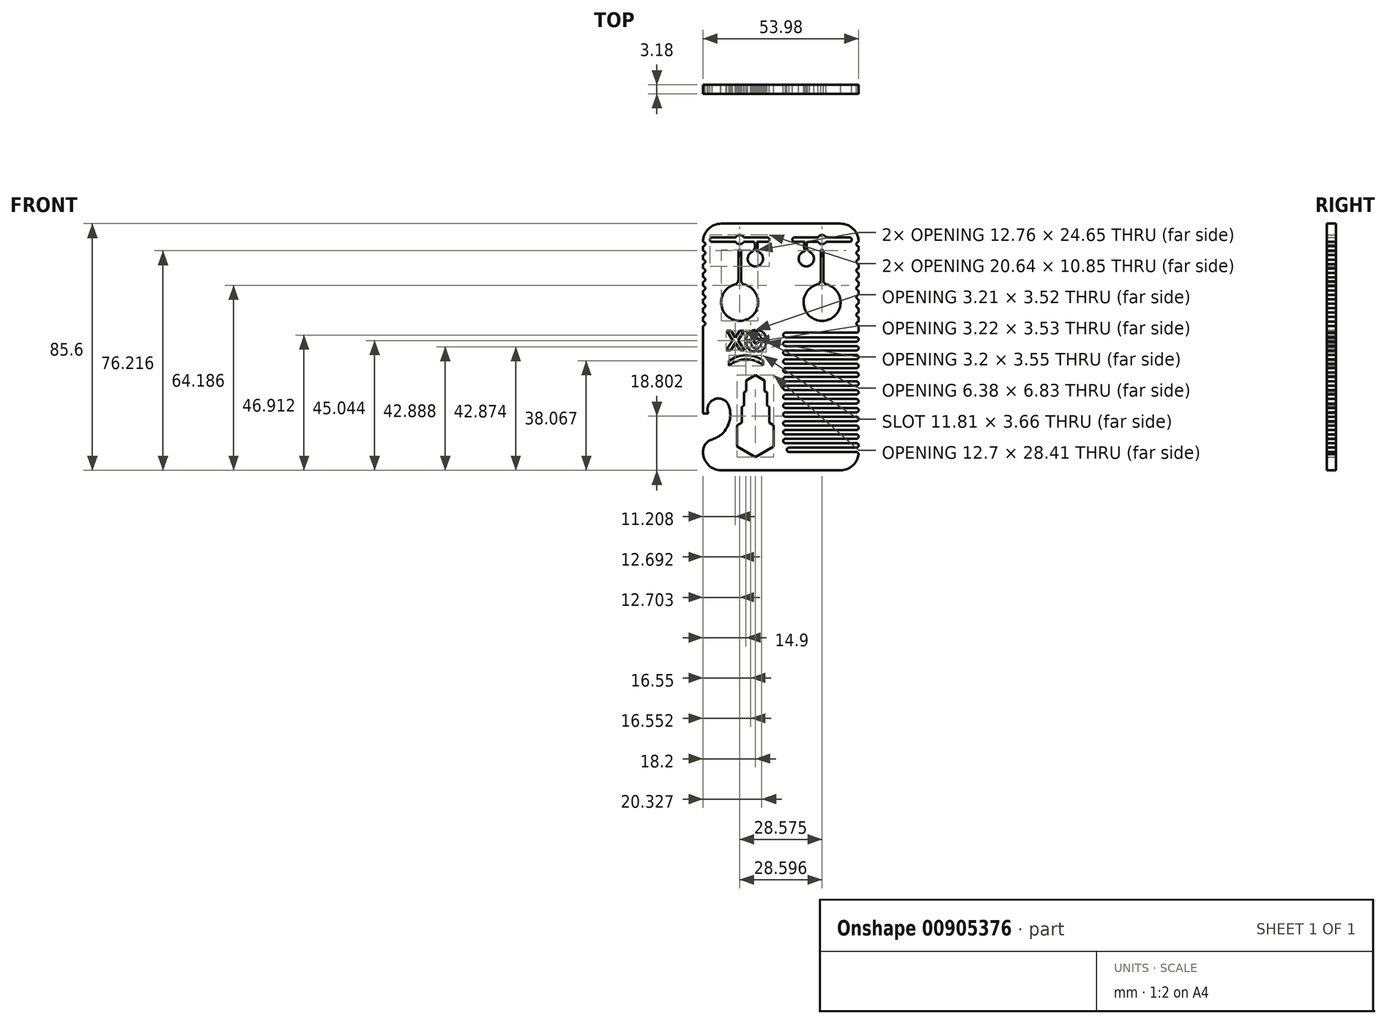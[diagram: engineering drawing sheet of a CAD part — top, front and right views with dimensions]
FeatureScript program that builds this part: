
annotation { "Feature Type Name" : "Feature", "Feature Type Description" : "" }
export const myFeature = defineFeature(function(context is Context, id is Id, definition is map)
    precondition{}
    {
        {
            var Q0;
            Q0=qCreatedBy(makeId("Front.planeOp"),FACE);
            var sketch = newSketch(context, id + "F0", { "sketchPlane" : qUnion([Q0])});
            skLineSegment(sketch, "E0.bottom", {"start": v(-17.87, 77.8) * mm, "end": v(23.4, 77.8) * mm});
            skLineSegment(sketch, "E0.top", {"start": v(-99.66, -7.8) * mm, "end": v(-99.66, -7.58) * mm});
            skLineSegment(sketch, "E0.left", {"start": v(-24.22, 69.91) * mm, "end": v(-24.22, 68.38) * mm});
            skLineSegment(sketch, "E0.right", {"start": v(29.76, 69.91) * mm, "end": v(29.76, 68.38) * mm});
            skPoint(sketch, "E1.visualSharp", {"position": v(-45.91, 65.1) * mm});
            skArc(sketch, "E1.filletArc", {"start": v(-17.87, 77.8) * mm, "mid": v(-22.36, 75.94) * mm, "end": v(-24.22, 71.45) * mm});
            skArc(sketch, "E2.filletArc", {"start": v(29.76, 71.45) * mm, "mid": v(27.9, 75.94) * mm, "end": v(23.4, 77.8) * mm});
            skPoint(sketch, "E3.visualSharp", {"position": v(29.76, -7.8) * mm});
            skArc(sketch, "E3.filletArc", {"start": v(23.4, -7.8) * mm, "mid": v(27.65, -6.17) * mm, "end": v(29.72, -2.12) * mm});
            skPoint(sketch, "E4.visualSharp", {"position": v(-24.22, -7.8) * mm});
            skArc(sketch, "E4.filletArc", {"start": v(-24.22, -1.45) * mm, "mid": v(-22.36, -5.94) * mm, "end": v(-17.87, -7.8) * mm});
            skLineSegment(sketch, "E5", {"start": v(-21.04, 71.45) * mm, "end": v(-21.04, 72.24) * mm});
            skLineSegment(sketch, "E6", {"start": v(-21.04, 73.03) * mm, "end": v(-13.12, 73.03) * mm});
            skLineSegment(sketch, "E7", {"start": v(-2, 72.24) * mm, "end": v(-2, 71.45) * mm});
            skPoint(sketch, "E8.center.orphan", {"position": v(2.77, -7.8) * mm});
            skLineSegment(sketch, "E9", {"start": v(-21.04, 71.45) * mm, "end": v(-12.9, 71.45) * mm});
            skLineSegment(sketch, "E10.trimOffspring", {"start": v(-4.44, -7.8) * mm, "end": v(23.4, -7.8) * mm});
            skArc(sketch, "E11", {"start": v(74.74, 43.3) * mm, "mid": v(66.07, 45.82) * mm, "end": v(57.48, 43.05) * mm});
            skLineSegment(sketch, "E12.MirrorCS", {"start": v(-10.76, 60.6) * mm, "end": v(-10.76, 60.6) * mm});
            skLineSegment(sketch, "E13.MirrorCS", {"start": v(-12.3, 60.6) * mm, "end": v(-12.3, 60.6) * mm});
            skArc(sketch, "E14", {"start": v(69.27, 55.85) * mm, "mid": v(68.77, 54.72) * mm, "end": v(68.53, 53.5) * mm});
            skArc(sketch, "E15", {"start": v(68.72, 51.54) * mm, "mid": v(69.46, 50.16) * mm, "end": v(70.87, 49.5) * mm});
            skArc(sketch, "E16", {"start": v(70.87, 58.64) * mm, "mid": v(70.16, 58.57) * mm, "end": v(69.47, 58.42) * mm});
            skArc(sketch, "E17", {"start": v(69.47, 58.42) * mm, "mid": v(68.6, 58.07) * mm, "end": v(67.84, 57.55) * mm});
            skArc(sketch, "E18", {"start": v(67.84, 57.55) * mm, "mid": v(67.12, 56.76) * mm, "end": v(66.62, 55.81) * mm});
            skArc(sketch, "E19", {"start": v(66.62, 55.81) * mm, "mid": v(66.3, 54.68) * mm, "end": v(66.18, 53.5) * mm});
            skArc(sketch, "E20", {"start": v(66.18, 53.5) * mm, "mid": v(66.18, 53.5) * mm, "end": v(66.18, 53.5) * mm});
            skArc(sketch, "E21", {"start": v(66.25, 51.87) * mm, "mid": v(66.4, 51.1) * mm, "end": v(66.64, 50.36) * mm});
            skArc(sketch, "E22", {"start": v(66.64, 50.36) * mm, "mid": v(66.92, 49.77) * mm, "end": v(67.29, 49.24) * mm});
            skArc(sketch, "E23", {"start": v(67.29, 49.24) * mm, "mid": v(67.8, 48.7) * mm, "end": v(68.4, 48.27) * mm});
            skArc(sketch, "E24", {"start": v(68.4, 48.27) * mm, "mid": v(69.1, 47.94) * mm, "end": v(69.84, 47.73) * mm});
            skArc(sketch, "E25", {"start": v(69.84, 47.73) * mm, "mid": v(70.31, 47.64) * mm, "end": v(70.8, 47.6) * mm});
            skArc(sketch, "E26", {"start": v(70.8, 47.6) * mm, "mid": v(70.83, 47.6) * mm, "end": v(70.87, 47.6) * mm});
            skLineSegment(sketch, "E27", {"start": v(71.26, 56.74) * mm, "end": v(71.26, 56.75) * mm});
            skLineSegment(sketch, "E28", {"start": v(71.28, 49.47) * mm, "end": v(71.28, 49.46) * mm});
            skLineSegment(sketch, "E29.trimOffspring", {"start": v(70.87, 56.7) * mm, "end": v(70.87, 58.65) * mm});
            skLineSegment(sketch, "E30", {"start": v(70.87, 48.55) * mm, "end": v(70.87, 47.6) * mm});
            skArc(sketch, "E31.trimOffspring", {"start": v(71.28, 47.58) * mm, "mid": v(71.3, 47.58) * mm, "end": v(71.3, 47.58) * mm});
            skLineSegment(sketch, "E32.trimOffspring", {"start": v(70.87, 49.5) * mm, "end": v(70.87, 48.55) * mm});
            skArc(sketch, "E33.trimOffspring", {"start": v(70.87, 56.7) * mm, "mid": v(70, 56.42) * mm, "end": v(69.27, 55.85) * mm});
            skPoint(sketch, "E34.orphan", {"position": v(68.51, 52.97) * mm});
            skLineSegment(sketch, "E35", {"start": v(71.26, 56.75) * mm, "end": v(71.26, 56.74) * mm});
            skArc(sketch, "E36.MirrorCS", {"start": v(71.64, 56.71) * mm, "mid": v(72.52, 56.43) * mm, "end": v(73.25, 55.87) * mm});
            skArc(sketch, "E37.MirrorCS", {"start": v(73.25, 55.87) * mm, "mid": v(73.77, 54.75) * mm, "end": v(74.01, 53.53) * mm});
            skArc(sketch, "E38.MirrorCS", {"start": v(73.84, 51.56) * mm, "mid": v(73.12, 50.17) * mm, "end": v(71.7, 49.5) * mm});
            skArc(sketch, "E39.MirrorCS", {"start": v(71.8, 47.6) * mm, "mid": v(71.77, 47.6) * mm, "end": v(71.73, 47.6) * mm});
            skArc(sketch, "E40.MirrorCS", {"start": v(72.76, 47.74) * mm, "mid": v(72.29, 47.65) * mm, "end": v(71.8, 47.6) * mm});
            skArc(sketch, "E41.MirrorCS", {"start": v(74.19, 48.3) * mm, "mid": v(73.5, 47.96) * mm, "end": v(72.76, 47.74) * mm});
            skArc(sketch, "E42.MirrorCS", {"start": v(75.3, 49.28) * mm, "mid": v(74.79, 48.73) * mm, "end": v(74.19, 48.3) * mm});
            skArc(sketch, "E43.MirrorCS", {"start": v(75.94, 50.4) * mm, "mid": v(75.66, 49.81) * mm, "end": v(75.3, 49.28) * mm});
            skArc(sketch, "E44.MirrorCS", {"start": v(76.3, 51.92) * mm, "mid": v(76.17, 51.15) * mm, "end": v(75.94, 50.4) * mm});
            skArc(sketch, "E45.MirrorCS", {"start": v(76.37, 53.55) * mm, "mid": v(76.37, 53.55) * mm, "end": v(76.37, 53.54) * mm});
            skArc(sketch, "E46.MirrorCS", {"start": v(75.9, 55.86) * mm, "mid": v(76.23, 54.73) * mm, "end": v(76.37, 53.55) * mm});
            skArc(sketch, "E47.MirrorCS", {"start": v(74.66, 57.58) * mm, "mid": v(75.39, 56.8) * mm, "end": v(75.9, 55.86) * mm});
            skArc(sketch, "E48.MirrorCS", {"start": v(73.02, 58.43) * mm, "mid": v(73.9, 58.1) * mm, "end": v(74.66, 57.58) * mm});
            skArc(sketch, "E49.MirrorCS", {"start": v(71.63, 58.65) * mm, "mid": v(72.33, 58.58) * mm, "end": v(73.02, 58.43) * mm});
            skLineSegment(sketch, "E50.MirrorCS", {"start": v(71.64, 56.71) * mm, "end": v(71.63, 58.65) * mm});
            skLineSegment(sketch, "E51.MirrorCS", {"start": v(71.7, 49.5) * mm, "end": v(71.72, 48.55) * mm});
            skLineSegment(sketch, "E52.MirrorCS", {"start": v(71.72, 48.55) * mm, "end": v(71.73, 47.6) * mm});
            skArc(sketch, "E53", {"start": v(71.28, 49.46) * mm, "mid": v(71.29, 49.46) * mm, "end": v(71.3, 49.46) * mm});
            skLineSegment(sketch, "E54.0", {"start": v(66.17, 52.73) * mm, "end": v(68.52, 52.75) * mm});
            skLineSegment(sketch, "E55.0", {"start": v(66.16, 53.5) * mm, "end": v(68.53, 53.5) * mm});
            skLineSegment(sketch, "E56.trimOffspring", {"start": v(74.01, 53.53) * mm, "end": v(76.38, 53.55) * mm});
            skPoint(sketch, "E57.orphan", {"position": v(71.27, 53.12) * mm});
            skLineSegment(sketch, "E58.trimOffspring", {"start": v(74.03, 52.77) * mm, "end": v(76.38, 52.78) * mm});
            skPoint(sketch, "E59.MirrorCS.end.orphan", {"position": v(71.3, 49.46) * mm});
            skPoint(sketch, "E59.MirrorCS.start.orphan", {"position": v(71.7, 49.5) * mm});
            skPoint(sketch, "E60.MirrorCS.end.orphan", {"position": v(72.06, 47.58) * mm});
            skPoint(sketch, "E60.MirrorCS.start.orphan", {"position": v(72.49, 47.6) * mm});
            skPoint(sketch, "E61.orphan", {"position": v(71.25, 58.65) * mm});
            skPoint(sketch, "E62.MirrorCS.end.orphan", {"position": v(71.64, 56.71) * mm});
            skArc(sketch, "E63.trimOffspring", {"start": v(66.17, 52.73) * mm, "mid": v(66.2, 52.3) * mm, "end": v(66.25, 51.87) * mm});
            skArc(sketch, "E64.trimOffspring", {"start": v(68.52, 52.75) * mm, "mid": v(68.59, 52.14) * mm, "end": v(68.72, 51.54) * mm});
            skArc(sketch, "E65.trimOffspring", {"start": v(74.03, 52.77) * mm, "mid": v(73.97, 52.16) * mm, "end": v(73.84, 51.56) * mm});
            skArc(sketch, "E66.trimOffspring", {"start": v(76.38, 52.78) * mm, "mid": v(76.36, 52.35) * mm, "end": v(76.3, 51.92) * mm});
            skText(sketch, "E67", { "text": "X", "fontName": "OpenSans-Bold.ttf"});
            skArc(sketch, "E68", {"start": v(-101.45, 5.62) * mm, "mid": v(-103.88, 10.61) * mm, "end": v(-108.72, 7.88) * mm});
            skArc(sketch, "E69", {"start": v(-99.66, -7.58) * mm, "mid": v(-100.52, -4.97) * mm, "end": v(-102.78, -3.42) * mm});
            skArc(sketch, "E70", {"start": v(-108.72, 7.88) * mm, "mid": v(-108.7, 2.5) * mm, "end": v(-105.7, -1.96) * mm});
            skArc(sketch, "E71", {"start": v(-105.7, -1.96) * mm, "mid": v(-104.29, -2.8) * mm, "end": v(-102.78, -3.42) * mm});
            skLineSegment(sketch, "E72", {"start": v(-101.45, 5.62) * mm, "end": v(-99.66, 5.62) * mm});
            skLineSegment(sketch, "E73", {"start": v(-10.77, 56.83) * mm, "end": v(-10.76, 56.83) * mm});
            skLineSegment(sketch, "E74", {"start": v(29.76, 41.39) * mm, "end": v(29.76, 42.32) * mm});
            skLineSegment(sketch, "E75", {"start": v(5.61, 0.07) * mm, "end": v(29, 0.07) * mm});
            skArc(sketch, "E76", {"start": v(29, 0.07) * mm, "mid": v(29.76, 0.84) * mm, "end": v(29, 1.6) * mm});
            skLineSegment(sketch, "E77", {"start": v(29, 1.6) * mm, "end": v(4.36, 1.6) * mm});
            skArc(sketch, "E78", {"start": v(29.72, -2.12) * mm, "mid": v(29.49, -1.65) * mm, "end": v(29, -1.46) * mm});
            skPoint(sketch, "E79.start.orphan", {"position": v(29.76, -1.45) * mm});
            skArc(sketch, "E80", {"start": v(5.61, 0.07) * mm, "mid": v(4.86, -0.7) * mm, "end": v(5.61, -1.46) * mm});
            skLineSegment(sketch, "E81", {"start": v(5.61, -1.46) * mm, "end": v(29, -1.46) * mm});
            skArc(sketch, "E82", {"start": v(4.36, 3.14) * mm, "mid": v(3.6, 2.37) * mm, "end": v(4.36, 1.6) * mm});
            skLineSegment(sketch, "E83", {"start": v(4.36, 3.14) * mm, "end": v(29, 3.14) * mm});
            skArc(sketch, "E84", {"start": v(29, 3.14) * mm, "mid": v(29.76, 3.9) * mm, "end": v(29, 4.67) * mm});
            skLineSegment(sketch, "E85", {"start": v(29, 4.67) * mm, "end": v(4.36, 4.67) * mm});
            skLineSegment(sketch, "E86", {"start": v(4.36, 6.2) * mm, "end": v(29, 6.2) * mm});
            skArc(sketch, "E87", {"start": v(29, 6.2) * mm, "mid": v(29.76, 6.97) * mm, "end": v(29, 7.74) * mm});
            skLineSegment(sketch, "E88", {"start": v(29, 7.74) * mm, "end": v(4.36, 7.74) * mm});
            skArc(sketch, "E89", {"start": v(4.36, 9.27) * mm, "mid": v(3.6, 8.5) * mm, "end": v(4.36, 7.74) * mm});
            skLineSegment(sketch, "E90", {"start": v(4.36, 9.27) * mm, "end": v(29, 9.27) * mm});
            skArc(sketch, "E91", {"start": v(29, 9.27) * mm, "mid": v(29.76, 10.04) * mm, "end": v(29, 10.8) * mm});
            skLineSegment(sketch, "E92", {"start": v(29, 10.8) * mm, "end": v(4.36, 10.8) * mm});
            skLineSegment(sketch, "E93", {"start": v(4.36, 12.34) * mm, "end": v(29, 12.34) * mm});
            skArc(sketch, "E94", {"start": v(29, 12.34) * mm, "mid": v(29.76, 13.1) * mm, "end": v(29, 13.87) * mm});
            skLineSegment(sketch, "E95", {"start": v(29, 13.87) * mm, "end": v(4.36, 13.87) * mm});
            skArc(sketch, "E96", {"start": v(4.36, 12.34) * mm, "mid": v(3.6, 11.57) * mm, "end": v(4.36, 10.8) * mm});
            skArc(sketch, "E97", {"start": v(4.36, 15.4) * mm, "mid": v(3.6, 14.64) * mm, "end": v(4.36, 13.87) * mm});
            skLineSegment(sketch, "E98", {"start": v(4.36, 15.4) * mm, "end": v(29, 15.4) * mm});
            skArc(sketch, "E99", {"start": v(29, 15.4) * mm, "mid": v(29.76, 16.17) * mm, "end": v(29, 16.94) * mm});
            skLineSegment(sketch, "E100", {"start": v(29, 16.94) * mm, "end": v(4.36, 16.94) * mm});
            skArc(sketch, "E101", {"start": v(4.36, 18.47) * mm, "mid": v(3.6, 17.7) * mm, "end": v(4.36, 16.94) * mm});
            skLineSegment(sketch, "E102", {"start": v(4.36, 18.47) * mm, "end": v(29, 18.47) * mm});
            skArc(sketch, "E103", {"start": v(29, 18.47) * mm, "mid": v(29.76, 19.24) * mm, "end": v(29, 20) * mm});
            skLineSegment(sketch, "E104", {"start": v(29, 20) * mm, "end": v(4.36, 20) * mm});
            skArc(sketch, "E105", {"start": v(4.36, 21.53) * mm, "mid": v(3.6, 20.77) * mm, "end": v(4.36, 20) * mm});
            skLineSegment(sketch, "E106", {"start": v(4.36, 21.53) * mm, "end": v(29, 21.53) * mm});
            skArc(sketch, "E107", {"start": v(29, 21.53) * mm, "mid": v(29.76, 22.3) * mm, "end": v(29, 23.07) * mm});
            skLineSegment(sketch, "E108", {"start": v(29, 23.07) * mm, "end": v(4.36, 23.07) * mm});
            skArc(sketch, "E109", {"start": v(4.36, 24.6) * mm, "mid": v(3.6, 23.83) * mm, "end": v(4.36, 23.07) * mm});
            skLineSegment(sketch, "E110", {"start": v(4.36, 24.6) * mm, "end": v(29, 24.6) * mm});
            skArc(sketch, "E111", {"start": v(29, 24.6) * mm, "mid": v(29.76, 25.37) * mm, "end": v(29, 26.13) * mm});
            skLineSegment(sketch, "E112", {"start": v(29, 26.13) * mm, "end": v(4.36, 26.13) * mm});
            skArc(sketch, "E113", {"start": v(4.36, 27.67) * mm, "mid": v(3.6, 26.9) * mm, "end": v(4.36, 26.13) * mm});
            skLineSegment(sketch, "E114", {"start": v(4.36, 27.67) * mm, "end": v(29, 27.67) * mm});
            skArc(sketch, "E115", {"start": v(29, 27.67) * mm, "mid": v(29.76, 28.43) * mm, "end": v(29, 29.2) * mm});
            skLineSegment(sketch, "E116", {"start": v(29, 29.2) * mm, "end": v(4.36, 29.2) * mm});
            skArc(sketch, "E117", {"start": v(4.36, 30.73) * mm, "mid": v(3.6, 29.97) * mm, "end": v(4.36, 29.2) * mm});
            skLineSegment(sketch, "E118", {"start": v(4.36, 30.73) * mm, "end": v(29, 30.73) * mm});
            skArc(sketch, "E119", {"start": v(29, 30.73) * mm, "mid": v(29.76, 31.5) * mm, "end": v(29, 32.26) * mm});
            skLineSegment(sketch, "E120", {"start": v(29, 32.26) * mm, "end": v(4.36, 32.26) * mm});
            skArc(sketch, "E121", {"start": v(4.36, 33.8) * mm, "mid": v(3.6, 33.03) * mm, "end": v(4.36, 32.26) * mm});
            skLineSegment(sketch, "E122", {"start": v(4.36, 33.8) * mm, "end": v(29, 33.8) * mm});
            skArc(sketch, "E123", {"start": v(29, 33.8) * mm, "mid": v(29.76, 34.56) * mm, "end": v(29, 35.33) * mm});
            skLineSegment(sketch, "E124", {"start": v(29, 35.33) * mm, "end": v(4.36, 35.33) * mm});
            skArc(sketch, "E125", {"start": v(4.36, 36.86) * mm, "mid": v(3.6, 36.1) * mm, "end": v(4.36, 35.33) * mm});
            skLineSegment(sketch, "E126", {"start": v(4.36, 36.86) * mm, "end": v(29, 36.86) * mm});
            skArc(sketch, "E127", {"start": v(29, 36.86) * mm, "mid": v(29.76, 37.63) * mm, "end": v(29, 38.4) * mm});
            skLineSegment(sketch, "E128", {"start": v(29, 38.4) * mm, "end": v(4.36, 38.4) * mm});
            skArc(sketch, "E129", {"start": v(4.36, 39.93) * mm, "mid": v(3.6, 39.16) * mm, "end": v(4.36, 38.4) * mm});
            skLineSegment(sketch, "E130", {"start": v(4.36, 39.93) * mm, "end": v(29, 39.93) * mm});
            skArc(sketch, "E131", {"start": v(29, 39.93) * mm, "mid": v(29.54, 40.16) * mm, "end": v(29.76, 40.7) * mm});
            skLineSegment(sketch, "E132", {"start": v(29.76, 40.7) * mm, "end": v(29.76, 41.39) * mm});
            skLineSegment(sketch, "E133.0", {"start": v(-11.98, 68.27) * mm, "end": v(-11.98, 58.2) * mm});
            skLineSegment(sketch, "E134.0", {"start": v(-11.09, 68.27) * mm, "end": v(-11.09, 58.2) * mm});
            skArc(sketch, "E135", {"start": v(-12.9, 56.75) * mm, "mid": v(-11.52, 44.06) * mm, "end": v(-10.16, 56.75) * mm});
            skArc(sketch, "E136", {"start": v(-24.22, 42.32) * mm, "mid": v(-23.46, 43.09) * mm, "end": v(-24.22, 43.85) * mm});
            skArc(sketch, "E137", {"start": v(-24.22, 45.39) * mm, "mid": v(-23.46, 46.15) * mm, "end": v(-24.22, 46.92) * mm});
            skArc(sketch, "E138", {"start": v(-24.22, 48.45) * mm, "mid": v(-23.46, 49.22) * mm, "end": v(-24.22, 49.99) * mm});
            skArc(sketch, "E139", {"start": v(-24.22, 51.52) * mm, "mid": v(-23.46, 52.28) * mm, "end": v(-24.22, 53.05) * mm});
            skArc(sketch, "E140", {"start": v(-24.22, 54.58) * mm, "mid": v(-23.46, 55.35) * mm, "end": v(-24.22, 56.12) * mm});
            skArc(sketch, "E141", {"start": v(-24.22, 57.65) * mm, "mid": v(-23.46, 58.42) * mm, "end": v(-24.22, 59.18) * mm});
            skArc(sketch, "E142", {"start": v(-24.22, 60.72) * mm, "mid": v(-23.46, 61.48) * mm, "end": v(-24.22, 62.25) * mm});
            skArc(sketch, "E143", {"start": v(-24.22, 63.78) * mm, "mid": v(-23.46, 64.55) * mm, "end": v(-24.22, 65.31) * mm});
            skArc(sketch, "E144", {"start": v(-24.22, 66.85) * mm, "mid": v(-23.46, 67.61) * mm, "end": v(-24.22, 68.38) * mm});
            skArc(sketch, "E145", {"start": v(-24.22, 69.91) * mm, "mid": v(-23.46, 70.68) * mm, "end": v(-24.22, 71.45) * mm});
            skArc(sketch, "E146", {"start": v(29.76, 43.85) * mm, "mid": v(29, 43.09) * mm, "end": v(29.76, 42.32) * mm});
            skArc(sketch, "E147", {"start": v(29.76, 46.92) * mm, "mid": v(29, 46.15) * mm, "end": v(29.76, 45.39) * mm});
            skArc(sketch, "E148", {"start": v(29.76, 49.99) * mm, "mid": v(29, 49.22) * mm, "end": v(29.76, 48.45) * mm});
            skArc(sketch, "E149", {"start": v(29.76, 53.05) * mm, "mid": v(29, 52.28) * mm, "end": v(29.76, 51.52) * mm});
            skArc(sketch, "E150", {"start": v(29.76, 56.12) * mm, "mid": v(29, 55.35) * mm, "end": v(29.76, 54.58) * mm});
            skArc(sketch, "E151", {"start": v(29.76, 59.18) * mm, "mid": v(29, 58.42) * mm, "end": v(29.76, 57.65) * mm});
            skArc(sketch, "E152", {"start": v(29.76, 62.25) * mm, "mid": v(29, 61.48) * mm, "end": v(29.76, 60.72) * mm});
            skArc(sketch, "E153", {"start": v(29.76, 65.31) * mm, "mid": v(29, 64.55) * mm, "end": v(29.76, 63.78) * mm});
            skArc(sketch, "E154", {"start": v(29.76, 68.38) * mm, "mid": v(29, 67.61) * mm, "end": v(29.76, 66.85) * mm});
            skArc(sketch, "E155", {"start": v(29.76, 71.45) * mm, "mid": v(29, 70.68) * mm, "end": v(29.76, 69.91) * mm});
            skLineSegment(sketch, "E156.trimOffspring", {"start": v(-24.22, 45.39) * mm, "end": v(-24.22, 43.85) * mm});
            skLineSegment(sketch, "E157.trimOffspring", {"start": v(-24.22, 48.45) * mm, "end": v(-24.22, 46.92) * mm});
            skLineSegment(sketch, "E158.trimOffspring", {"start": v(-24.22, 51.52) * mm, "end": v(-24.22, 49.99) * mm});
            skLineSegment(sketch, "E159.trimOffspring", {"start": v(-24.22, 54.58) * mm, "end": v(-24.22, 53.05) * mm});
            skLineSegment(sketch, "E160.trimOffspring", {"start": v(-24.22, 57.65) * mm, "end": v(-24.22, 56.12) * mm});
            skLineSegment(sketch, "E161.trimOffspring", {"start": v(-24.22, 60.72) * mm, "end": v(-24.22, 59.18) * mm});
            skLineSegment(sketch, "E162.trimOffspring", {"start": v(-24.22, 63.78) * mm, "end": v(-24.22, 62.25) * mm});
            skLineSegment(sketch, "E163.trimOffspring", {"start": v(-24.22, 66.85) * mm, "end": v(-24.22, 65.31) * mm});
            skLineSegment(sketch, "E164.trimOffspring", {"start": v(29.76, 66.85) * mm, "end": v(29.76, 65.31) * mm});
            skLineSegment(sketch, "E165.trimOffspring", {"start": v(29.76, 63.78) * mm, "end": v(29.76, 62.25) * mm});
            skLineSegment(sketch, "E166.trimOffspring", {"start": v(29.76, 60.72) * mm, "end": v(29.76, 59.18) * mm});
            skLineSegment(sketch, "E167.trimOffspring", {"start": v(29.76, 57.65) * mm, "end": v(29.76, 56.12) * mm});
            skLineSegment(sketch, "E168.trimOffspring", {"start": v(29.76, 54.58) * mm, "end": v(29.76, 53.05) * mm});
            skLineSegment(sketch, "E169.trimOffspring", {"start": v(29.76, 51.52) * mm, "end": v(29.76, 49.99) * mm});
            skLineSegment(sketch, "E170.trimOffspring", {"start": v(29.76, 48.45) * mm, "end": v(29.76, 46.92) * mm});
            skLineSegment(sketch, "E171.trimOffspring", {"start": v(29.76, 45.39) * mm, "end": v(29.76, 43.85) * mm});
            skLineSegment(sketch, "E172", {"start": v(74.74, 40.78) * mm, "end": v(74.74, 43.3) * mm});
            skLineSegment(sketch, "E173", {"start": v(74.74, 43.3) * mm, "end": v(74.74, 40.78) * mm});
            skCircle(sketch, "E174", {"center": v(71.27, 53.12) * mm, "radius": 1.3 * mm});
            skPoint(sketch, "E175.orphan", {"position": v(-11.53, 68.27) * mm});
            skLineSegment(sketch, "E176.trimOffspring", {"start": v(-9.94, 73.03) * mm, "end": v(-2, 73.03) * mm});
            skLineSegment(sketch, "E177", {"start": v(-13.12, 73.03) * mm, "end": v(-12.9, 73.03) * mm});
            skArc(sketch, "E178.MirrorCS", {"start": v(-12.9, 73.03) * mm, "mid": v(-11.52, 73.84) * mm, "end": v(-10.13, 73.03) * mm});
            skArc(sketch, "E179.MirrorCS", {"start": v(-10.13, 71.45) * mm, "mid": v(-11.52, 70.64) * mm, "end": v(-12.9, 71.45) * mm});
            skPoint(sketch, "E180.start.orphan", {"position": v(2.77, 77.8) * mm});
            skLineSegment(sketch, "E181.trimOffspring", {"start": v(-10.13, 71.45) * mm, "end": v(-6.5, 71.45) * mm});
            skLineSegment(sketch, "E182.trimOffspring", {"start": v(-10.13, 73.03) * mm, "end": v(-9.94, 73.03) * mm});
            skLineSegment(sketch, "E183.trimOffspring", {"start": v(-5.52, 71.45) * mm, "end": v(-2, 71.45) * mm});
            skArc(sketch, "E184", {"start": v(-7.14, 68.04) * mm, "mid": v(-6.18, 69.62) * mm, "end": v(-6.5, 71.45) * mm});
            skArc(sketch, "E185.0", {"start": v(-5.63, 68.52) * mm, "mid": v(-5.25, 69.97) * mm, "end": v(-5.52, 71.45) * mm});
            skPoint(sketch, "E186.start.orphan", {"position": v(-7.14, 68.04) * mm});
            skArc(sketch, "E187.MirrorCS", {"start": v(-7.14, 68.04) * mm, "mid": v(-5.8, 63) * mm, "end": v(-5.48, 68.2) * mm});
            skPoint(sketch, "E188.orphan", {"position": v(-7.17, 68.02) * mm});
            skArc(sketch, "E189.0", {"start": v(74.74, 40.78) * mm, "mid": v(66.06, 43.78) * mm, "end": v(57.48, 40.47) * mm});
            skLineSegment(sketch, "E190", {"start": v(57.48, 43.05) * mm, "end": v(57.48, 40.47) * mm});
            skArc(sketch, "E191", {"start": v(-5.63, 68.52) * mm, "mid": v(-5.62, 68.32) * mm, "end": v(-5.48, 68.2) * mm});
            skLineSegment(sketch, "E192.0", {"start": v(-24.15, -14.77) * mm, "end": v(-19.6, -14.16) * mm});
            skLineSegment(sketch, "E192.1", {"start": v(-19.6, -14.16) * mm, "end": v(-16.8, -17.8) * mm});
            skArc(sketch, "E193", {"start": v(4.36, 6.2) * mm, "mid": v(3.6, 5.44) * mm, "end": v(4.36, 4.67) * mm});
            skLineSegment(sketch, "E194.0", {"start": v(0.33, 0.46) * mm, "end": v(-6.02, -3.2) * mm});
            skLineSegment(sketch, "E194.1", {"start": v(-6.02, -3.2) * mm, "end": v(-12.37, 0.46) * mm});
            skLineSegment(sketch, "E194.2", {"start": v(-12.37, 0.46) * mm, "end": v(-12.37, 7.8) * mm});
            skLineSegment(sketch, "E194.3", {"start": v(-12.37, 7.8) * mm, "end": v(-10.78, 8.71) * mm});
            skLineSegment(sketch, "E194.4", {"start": v(-1.26, 8.71) * mm, "end": v(0.33, 7.8) * mm});
            skLineSegment(sketch, "E194.5", {"start": v(0.33, 7.8) * mm, "end": v(0.33, 0.46) * mm});
            skPoint(sketch, "E194.0.midPoint", {"position": v(-2.84, -1.37) * mm});
            skLineSegment(sketch, "E195.2", {"start": v(-10.78, 8.71) * mm, "end": v(-10.78, 14.2) * mm});
            skLineSegment(sketch, "E195.3", {"start": v(-10.78, 14.2) * mm, "end": v(-9.99, 14.67) * mm});
            skLineSegment(sketch, "E195.4", {"start": v(-2.05, 14.67) * mm, "end": v(-1.26, 14.2) * mm});
            skLineSegment(sketch, "E195.5", {"start": v(-1.26, 14.2) * mm, "end": v(-1.26, 8.71) * mm});
            skPoint(sketch, "E195.0.midPoint", {"position": v(-3.64, 7.34) * mm});
            skPoint(sketch, "E196.visualSharp", {"position": v(-6.55, 6.45) * mm});
            skLineSegment(sketch, "E197.2", {"start": v(-9.99, 14.67) * mm, "end": v(-9.99, 19.25) * mm});
            skLineSegment(sketch, "E197.3", {"start": v(-9.99, 19.25) * mm, "end": v(-9.2, 19.7) * mm});
            skLineSegment(sketch, "E197.4", {"start": v(-2.84, 19.7) * mm, "end": v(-2.05, 19.25) * mm});
            skLineSegment(sketch, "E197.5", {"start": v(-2.05, 19.25) * mm, "end": v(-2.05, 14.67) * mm});
            skPoint(sketch, "E197.0.midPoint", {"position": v(-4.04, 13.52) * mm});
            skLineSegment(sketch, "E198.2", {"start": v(-9.2, 19.7) * mm, "end": v(-9.2, 23.38) * mm});
            skLineSegment(sketch, "E198.3", {"start": v(-9.2, 23.38) * mm, "end": v(-6.02, 25.2) * mm});
            skLineSegment(sketch, "E198.4", {"start": v(-6.02, 25.2) * mm, "end": v(-2.84, 23.38) * mm});
            skLineSegment(sketch, "E198.5", {"start": v(-2.84, 23.38) * mm, "end": v(-2.84, 19.7) * mm});
            skPoint(sketch, "E198.0.midPoint", {"position": v(-4.43, 18.8) * mm});
            skPoint(sketch, "E199.orphan", {"position": v(-6.02, 11.46) * mm});
            skPoint(sketch, "E200.orphan", {"position": v(-6.02, 16.96) * mm});
            skPoint(sketch, "E201.orphan", {"position": v(-6.02, 21.54) * mm});
            skLineSegment(sketch, "E202", {"start": v(-93, 23.24) * mm, "end": v(-93, -28.24) * mm});
            skLineSegment(sketch, "E203.MirrorCS", {"start": v(-24.22, -1.45) * mm, "end": v(-24.22, -1.23) * mm});
            skLineSegment(sketch, "E204.MirrorCS", {"start": v(-22.42, 11.97) * mm, "end": v(-24.22, 11.97) * mm});
            skArc(sketch, "E205.MirrorCS", {"start": v(-22.42, 11.97) * mm, "mid": v(-19.99, 16.96) * mm, "end": v(-15.16, 14.23) * mm});
            skArc(sketch, "E206.MirrorCS", {"start": v(-18.18, 4.39) * mm, "mid": v(-19.58, 3.56) * mm, "end": v(-21.09, 2.93) * mm});
            skArc(sketch, "E207.MirrorCS", {"start": v(-15.16, 14.23) * mm, "mid": v(-15.18, 8.85) * mm, "end": v(-18.18, 4.39) * mm});
            skArc(sketch, "E208.MirrorCS", {"start": v(-24.22, -1.23) * mm, "mid": v(-23.35, 1.38) * mm, "end": v(-21.09, 2.93) * mm});
            skLineSegment(sketch, "E209", {"start": v(-24.22, 11.97) * mm, "end": v(-24.22, 42.32) * mm});
            skLineSegment(sketch, "E210.0", {"start": v(-6.02, 21.54) * mm, "end": v(-4.43, 18.8) * mm, "construction": true});
            skLineSegment(sketch, "E211.0", {"start": v(-6.02, 11.46) * mm, "end": v(-3.64, 7.34) * mm, "construction": true});
            skLineSegment(sketch, "E212.0", {"start": v(-6.02, 16.96) * mm, "end": v(-4.04, 13.52) * mm, "construction": true});
            skLineSegment(sketch, "E213", {"start": v(-17.87, -7.8) * mm, "end": v(-4.44, -7.8) * mm});
            skArc(sketch, "E214.0", {"start": v(-3.41, 30.37) * mm, "mid": v(-9.35, 32.1) * mm, "end": v(-15.23, 30.2) * mm});
            skArc(sketch, "E214.1", {"start": v(-7.16, 38.96) * mm, "mid": v(-7.5, 38.19) * mm, "end": v(-7.67, 37.36) * mm});
            skArc(sketch, "E214.2", {"start": v(-7.53, 36.01) * mm, "mid": v(-7.03, 35.07) * mm, "end": v(-6.06, 34.6) * mm});
            skArc(sketch, "E214.3", {"start": v(-6.07, 40.87) * mm, "mid": v(-6.55, 40.82) * mm, "end": v(-7.02, 40.72) * mm});
            skArc(sketch, "E214.4", {"start": v(-7.02, 40.72) * mm, "mid": v(-7.61, 40.48) * mm, "end": v(-8.14, 40.12) * mm});
            skArc(sketch, "E214.5", {"start": v(-8.14, 40.12) * mm, "mid": v(-8.63, 39.58) * mm, "end": v(-8.97, 38.94) * mm});
            skArc(sketch, "E214.6", {"start": v(-8.97, 38.94) * mm, "mid": v(-9.2, 38.16) * mm, "end": v(-9.27, 37.36) * mm});
            skArc(sketch, "E214.7", {"start": v(-9.27, 37.36) * mm, "mid": v(-9.27, 37.35) * mm, "end": v(-9.28, 37.35) * mm});
            skArc(sketch, "E214.8", {"start": v(-9.23, 36.24) * mm, "mid": v(-9.13, 35.71) * mm, "end": v(-8.96, 35.2) * mm});
            skArc(sketch, "E214.9", {"start": v(-8.96, 35.2) * mm, "mid": v(-8.77, 34.8) * mm, "end": v(-8.52, 34.44) * mm});
            skArc(sketch, "E214.10", {"start": v(-8.52, 34.44) * mm, "mid": v(-8.16, 34.07) * mm, "end": v(-7.75, 33.77) * mm});
            skArc(sketch, "E214.11", {"start": v(-7.75, 33.77) * mm, "mid": v(-7.28, 33.55) * mm, "end": v(-6.77, 33.4) * mm});
            skArc(sketch, "E214.12", {"start": v(-6.77, 33.4) * mm, "mid": v(-6.45, 33.34) * mm, "end": v(-6.12, 33.31) * mm});
            skArc(sketch, "E214.13", {"start": v(-6.12, 33.31) * mm, "mid": v(-6.09, 33.31) * mm, "end": v(-6.06, 33.31) * mm});
            skLineSegment(sketch, "E214.14", {"start": v(-5.8, 39.57) * mm, "end": v(-5.8, 39.58) * mm});
            skLineSegment(sketch, "E214.15", {"start": v(-5.78, 34.6) * mm, "end": v(-5.78, 34.59) * mm});
            skLineSegment(sketch, "E214.16", {"start": v(-6.06, 39.55) * mm, "end": v(-6.07, 40.88) * mm});
            skLineSegment(sketch, "E214.17", {"start": v(-6.06, 33.96) * mm, "end": v(-6.06, 33.31) * mm});
            skArc(sketch, "E214.18", {"start": v(-5.78, 33.3) * mm, "mid": v(-5.78, 33.3) * mm, "end": v(-5.77, 33.3) * mm});
            skLineSegment(sketch, "E214.19", {"start": v(-6.06, 34.6) * mm, "end": v(-6.06, 33.96) * mm});
            skArc(sketch, "E214.20", {"start": v(-6.06, 39.55) * mm, "mid": v(-6.66, 39.35) * mm, "end": v(-7.16, 38.96) * mm});
            skPoint(sketch, "E214.21", {"position": v(-7.68, 36.99) * mm});
            skArc(sketch, "E214.22", {"start": v(-5.78, 33.3) * mm, "mid": v(-5.78, 33.3) * mm, "end": v(-5.77, 33.3) * mm});
            skLineSegment(sketch, "E214.23", {"start": v(-5.8, 39.58) * mm, "end": v(-5.8, 39.57) * mm});
            skArc(sketch, "E214.24", {"start": v(-5.54, 39.55) * mm, "mid": v(-4.94, 39.36) * mm, "end": v(-4.43, 38.98) * mm});
            skArc(sketch, "E214.25", {"start": v(-4.43, 38.98) * mm, "mid": v(-4.08, 38.2) * mm, "end": v(-3.91, 37.38) * mm});
            skArc(sketch, "E214.26", {"start": v(-4.03, 36.03) * mm, "mid": v(-4.53, 35.08) * mm, "end": v(-5.5, 34.61) * mm});
            skArc(sketch, "E214.27", {"start": v(-5.42, 33.32) * mm, "mid": v(-5.45, 33.32) * mm, "end": v(-5.48, 33.31) * mm});
            skArc(sketch, "E214.28", {"start": v(-4.77, 33.41) * mm, "mid": v(-5.1, 33.35) * mm, "end": v(-5.42, 33.32) * mm});
            skArc(sketch, "E214.29", {"start": v(-3.8, 33.8) * mm, "mid": v(-4.27, 33.56) * mm, "end": v(-4.77, 33.41) * mm});
            skArc(sketch, "E214.30", {"start": v(-3.03, 34.46) * mm, "mid": v(-3.38, 34.1) * mm, "end": v(-3.8, 33.8) * mm});
            skArc(sketch, "E214.31", {"start": v(-2.6, 35.23) * mm, "mid": v(-2.79, 34.83) * mm, "end": v(-3.03, 34.46) * mm});
            skArc(sketch, "E214.32", {"start": v(-2.34, 36.27) * mm, "mid": v(-2.44, 35.74) * mm, "end": v(-2.6, 35.23) * mm});
            skArc(sketch, "E214.33", {"start": v(-2.3, 37.39) * mm, "mid": v(-2.3, 37.39) * mm, "end": v(-2.3, 37.38) * mm});
            skArc(sketch, "E214.34", {"start": v(-2.62, 38.97) * mm, "mid": v(-2.4, 38.2) * mm, "end": v(-2.3, 37.39) * mm});
            skArc(sketch, "E214.35", {"start": v(-3.47, 40.15) * mm, "mid": v(-2.97, 39.6) * mm, "end": v(-2.62, 38.97) * mm});
            skArc(sketch, "E214.36", {"start": v(-4.6, 40.73) * mm, "mid": v(-4, 40.5) * mm, "end": v(-3.47, 40.15) * mm});
            skArc(sketch, "E214.37", {"start": v(-5.55, 40.88) * mm, "mid": v(-5.06, 40.83) * mm, "end": v(-4.6, 40.73) * mm});
            skLineSegment(sketch, "E214.38", {"start": v(-5.54, 39.55) * mm, "end": v(-5.55, 40.88) * mm});
            skLineSegment(sketch, "E214.39", {"start": v(-5.5, 34.61) * mm, "end": v(-5.49, 33.97) * mm});
            skLineSegment(sketch, "E214.40", {"start": v(-5.49, 33.97) * mm, "end": v(-5.48, 33.31) * mm});
            skArc(sketch, "E214.41", {"start": v(-5.78, 34.59) * mm, "mid": v(-5.78, 34.59) * mm, "end": v(-5.78, 34.59) * mm});
            skLineSegment(sketch, "E214.42", {"start": v(-9.28, 36.83) * mm, "end": v(-7.67, 36.84) * mm});
            skLineSegment(sketch, "E214.43", {"start": v(-9.28, 37.35) * mm, "end": v(-7.67, 37.36) * mm});
            skLineSegment(sketch, "E214.44", {"start": v(-3.91, 37.38) * mm, "end": v(-2.3, 37.38) * mm});
            skPoint(sketch, "E214.45", {"position": v(-5.79, 37.09) * mm});
            skLineSegment(sketch, "E214.46", {"start": v(-3.9, 36.85) * mm, "end": v(-2.3, 36.86) * mm});
            skPoint(sketch, "E214.47", {"position": v(-5.77, 34.59) * mm});
            skPoint(sketch, "E214.48", {"position": v(-5.5, 34.61) * mm});
            skPoint(sketch, "E214.49", {"position": v(-5.25, 33.3) * mm});
            skPoint(sketch, "E214.50", {"position": v(-4.96, 33.31) * mm});
            skPoint(sketch, "E214.51", {"position": v(-5.8, 40.88) * mm});
            skPoint(sketch, "E214.52", {"position": v(-5.8, 40.88) * mm});
            skPoint(sketch, "E214.53", {"position": v(-5.54, 39.55) * mm});
            skArc(sketch, "E214.54", {"start": v(-9.28, 36.83) * mm, "mid": v(-9.26, 36.53) * mm, "end": v(-9.23, 36.24) * mm});
            skArc(sketch, "E214.55", {"start": v(-7.67, 36.84) * mm, "mid": v(-7.63, 36.42) * mm, "end": v(-7.53, 36.01) * mm});
            skArc(sketch, "E214.56", {"start": v(-3.9, 36.85) * mm, "mid": v(-3.94, 36.44) * mm, "end": v(-4.03, 36.03) * mm});
            skArc(sketch, "E214.57", {"start": v(-2.3, 36.86) * mm, "mid": v(-2.31, 36.57) * mm, "end": v(-2.34, 36.27) * mm});
            skLineSegment(sketch, "E214.58", {"start": v(-3.41, 28.65) * mm, "end": v(-3.41, 30.37) * mm});
            skLineSegment(sketch, "E214.59", {"start": v(-3.41, 30.37) * mm, "end": v(-3.41, 28.65) * mm});
            skCircle(sketch, "E214.60", {"center": v(-5.79, 37.09) * mm, "radius": 0.89 * mm});
            skArc(sketch, "E214.61", {"start": v(-3.41, 28.65) * mm, "mid": v(-9.36, 30.7) * mm, "end": v(-15.23, 28.43) * mm});
            skLineSegment(sketch, "E214.62", {"start": v(-15.23, 30.2) * mm, "end": v(-15.23, 28.43) * mm});
            skLineSegment(sketch, "E215.0.0", {"start": v(-16.04, 40.66) * mm, "end": v(-13.9, 37.27) * mm});
            skLineSegment(sketch, "E215.0.1", {"start": v(-13.9, 37.27) * mm, "end": v(-16.2, 33.83) * mm});
            skLineSegment(sketch, "E215.0.2", {"start": v(-16.2, 33.83) * mm, "end": v(-14.55, 33.83) * mm});
            skLineSegment(sketch, "E215.0.3", {"start": v(-14.55, 33.83) * mm, "end": v(-12.96, 36.41) * mm});
            skLineSegment(sketch, "E215.0.4", {"start": v(-12.96, 36.41) * mm, "end": v(-11.37, 33.83) * mm});
            skLineSegment(sketch, "E215.0.5", {"start": v(-11.37, 33.83) * mm, "end": v(-9.82, 33.83) * mm});
            skLineSegment(sketch, "E215.0.6", {"start": v(-9.82, 33.83) * mm, "end": v(-12.09, 37.35) * mm});
            skLineSegment(sketch, "E215.0.7", {"start": v(-12.09, 37.35) * mm, "end": v(-9.97, 40.66) * mm});
            skLineSegment(sketch, "E215.0.8", {"start": v(-9.97, 40.66) * mm, "end": v(-11.56, 40.66) * mm});
            skLineSegment(sketch, "E215.0.9", {"start": v(-11.56, 40.66) * mm, "end": v(-13.04, 38.2) * mm});
            skLineSegment(sketch, "E215.0.10", {"start": v(-13.04, 38.2) * mm, "end": v(-14.48, 40.66) * mm});
            skLineSegment(sketch, "E215.0.11", {"start": v(-14.48, 40.66) * mm, "end": v(-16.04, 40.66) * mm});
            skArc(sketch, "E216", {"start": v(-12.9, 56.75) * mm, "mid": v(-12.25, 57.36) * mm, "end": v(-11.98, 58.2) * mm});
            skArc(sketch, "E217", {"start": v(-11.09, 68.27) * mm, "mid": v(-11.53, 68.7) * mm, "end": v(-11.98, 68.27) * mm});
            skArc(sketch, "E218.MirrorCS", {"start": v(-10.16, 56.75) * mm, "mid": v(-10.82, 57.36) * mm, "end": v(-11.09, 58.2) * mm});
            skLineSegment(sketch, "E219", {"start": v(2.77, 77.8) * mm, "end": v(2.77, 62.36) * mm, "construction": true});
            skArc(sketch, "E220.MirrorCS", {"start": v(16.63, 68.27) * mm, "mid": v(17.07, 68.7) * mm, "end": v(17.52, 68.27) * mm});
            skArc(sketch, "E221.MirrorCS", {"start": v(15.7, 56.75) * mm, "mid": v(16.36, 57.36) * mm, "end": v(16.63, 58.2) * mm});
            skLineSegment(sketch, "E222.MirrorCS", {"start": v(17.83, 60.6) * mm, "end": v(17.83, 60.6) * mm});
            skLineSegment(sketch, "E223.MirrorCS", {"start": v(16.3, 60.6) * mm, "end": v(16.3, 60.6) * mm});
            skLineSegment(sketch, "E224.MirrorCS", {"start": v(16.31, 56.83) * mm, "end": v(16.3, 56.83) * mm});
            skArc(sketch, "E225.MirrorCS", {"start": v(18.44, 56.75) * mm, "mid": v(17.79, 57.36) * mm, "end": v(17.52, 58.2) * mm});
            skLineSegment(sketch, "E226.MirrorCS", {"start": v(17.52, 68.27) * mm, "end": v(17.52, 58.2) * mm});
            skLineSegment(sketch, "E227.MirrorCS", {"start": v(16.63, 68.27) * mm, "end": v(16.63, 58.2) * mm});
            skArc(sketch, "E228.MirrorCS", {"start": v(18.44, 56.75) * mm, "mid": v(17.06, 44.06) * mm, "end": v(15.7, 56.75) * mm});
            skArc(sketch, "E229", {"start": v(-21.04, 73.03) * mm, "mid": v(-21.84, 72.24) * mm, "end": v(-21.04, 71.45) * mm});
            skArc(sketch, "E230", {"start": v(-2, 71.45) * mm, "mid": v(-1.2, 72.24) * mm, "end": v(-2, 73.03) * mm});
            skLineSegment(sketch, "E231.MirrorCS", {"start": v(18.66, 73.03) * mm, "end": v(18.45, 73.03) * mm});
            skLineSegment(sketch, "E232.MirrorCS", {"start": v(26.58, 71.45) * mm, "end": v(26.58, 72.24) * mm});
            skLineSegment(sketch, "E233.MirrorCS", {"start": v(7.53, 72.24) * mm, "end": v(7.53, 71.45) * mm});
            skLineSegment(sketch, "E234.MirrorCS", {"start": v(15.67, 73.03) * mm, "end": v(15.48, 73.03) * mm});
            skArc(sketch, "E235.MirrorCS", {"start": v(11.17, 68.52) * mm, "mid": v(11.17, 68.32) * mm, "end": v(11.02, 68.2) * mm});
            skPoint(sketch, "E236.MirrorP", {"position": v(12.7, 68.02) * mm});
            skPoint(sketch, "E237.MirrorP", {"position": v(12.68, 68.04) * mm});
            skArc(sketch, "E238.MirrorCS", {"start": v(18.45, 73.03) * mm, "mid": v(17.06, 73.84) * mm, "end": v(15.67, 73.03) * mm});
            skLineSegment(sketch, "E239.MirrorCS", {"start": v(11.06, 71.45) * mm, "end": v(7.53, 71.45) * mm});
            skLineSegment(sketch, "E240.MirrorCS", {"start": v(15.48, 73.03) * mm, "end": v(7.53, 73.03) * mm});
            skLineSegment(sketch, "E241.MirrorCS", {"start": v(15.67, 71.45) * mm, "end": v(12.05, 71.45) * mm});
            skArc(sketch, "E242.MirrorCS", {"start": v(12.68, 68.04) * mm, "mid": v(11.35, 63) * mm, "end": v(11.02, 68.2) * mm});
            skArc(sketch, "E243.MirrorCS", {"start": v(15.67, 71.45) * mm, "mid": v(17.06, 70.64) * mm, "end": v(18.45, 71.45) * mm});
            skArc(sketch, "E244.MirrorCS", {"start": v(7.53, 71.45) * mm, "mid": v(6.74, 72.24) * mm, "end": v(7.53, 73.03) * mm});
            skLineSegment(sketch, "E245.MirrorCS", {"start": v(26.58, 73.03) * mm, "end": v(18.66, 73.03) * mm});
            skLineSegment(sketch, "E246.MirrorCS", {"start": v(26.58, 71.45) * mm, "end": v(18.45, 71.45) * mm});
            skArc(sketch, "E247.MirrorCS", {"start": v(11.17, 68.52) * mm, "mid": v(10.8, 69.97) * mm, "end": v(11.06, 71.45) * mm});
            skArc(sketch, "E248.MirrorCS", {"start": v(12.68, 68.04) * mm, "mid": v(11.73, 69.62) * mm, "end": v(12.05, 71.45) * mm});
            skArc(sketch, "E249.MirrorCS", {"start": v(26.58, 73.03) * mm, "mid": v(27.38, 72.24) * mm, "end": v(26.58, 71.45) * mm});
            const initialGuessF0  = {"E67": [0.05515, 0.04835, 1, 0, 0.01006]};
            skSetInitialGuess(sketch, initialGuessF0);
            skSolve(sketch);
        }
        {
            var Q0;
            Q0=makeQuery(id+"F0.imprint","IMPRINT",FACE,{"disambiguationData":[TD([[makeQuery(id+"F0.imprint","IMPRINT",EDGE,{"derivedFrom":sQuery(id+"F0.wireOp",EDGE,"E0.bottom")}),-1.0]])]});
            extrude(context, id + "F1", {"entities" : qUnion([Q0]), "depth" : 3.17 * mm, "offsetDistance" : 25.4 * mm});
        }
    });
